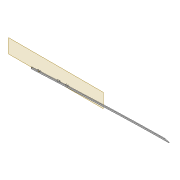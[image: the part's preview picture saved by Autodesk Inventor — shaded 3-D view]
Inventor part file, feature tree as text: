
AUTODESK INVENTOR PART (.ipt)
format: ipt  version: 2022 (Build 260153000, 153)  size: 629,760 bytes
history: native  units: mm
features: projected_geometry x9, extrude x8, sketch x8, fillet x2, shell x1, plane x1, chamfer x1
ambient origin geometry x8: Origin, YZ Plane, XZ Plane, XY Plane, X Axis, Y Axis, Z Axis, Center Point
bodies: Solid1 (feature_tree)
feature tree (30):
  extrude  "Extrusion1"  Depth=4.0mm
  shell  "Shell1"  Thickness=2.4mm
  extrude  "Extrusion8"  Depth=5.9mm
  extrude  "Extrusion3"  Depth=10.0mm TaperAngle=0.0deg
  extrude  "Extrusion4"  Depth=5.0mm
  fillet  "Fillet1"  Radius=5.0mm
  sketch  "Sketch10"  dims[d22=2.0mm d23=0.0mm d31=2.0mm d32=5.0mm]
  extrude  "Extrusion5"  Depth=2.5mm
  plane  "Work Plane2"
  extrude  "Extrusion9"  Depth=5.0mm
  fillet  "Fillet2"  Radius=2.5mm
  extrude  "Extrusion10"  Depth=6.0mm
  chamfer  "Chamfer1"  Distance=2.0mm
  extrude  "Extrusion13"  Depth=5.0mm
  sketch  "Sketch31"  dims[d37=5.0mm d38=2.0mm d40=2.5mm]
  sketch  "Sketch35"  dims[d66=3.0mm d67=12.0mm d68=5.0mm d69=45.0mm d70=12.0mm d71=3.05mm d72=10.0mm d73=0.0mm d74=2.0mm d75=100.0mm d76=20.0mm d77=0.5mm d78=10.0mm d79=0.0mm d109=45.0deg d129=3.0mm d130=2.0mm d131=45.0deg d132=1.0mm d133=1.0mm d134=10.0mm d135=0.0mm d136=1.0mm d137=1.0mm d138=1.0mm d139=1.0mm d140=20.0mm]
  sketch  "Sketch3"  dims[d0=2.0mm d1=0.0mm d2=4.0mm d7=2.4mm]
  sketch  "Sketch8"  dims[d8=2.4mm d9=5.9mm]
  sketch  "Sketch9"  dims[d13=10.0mm d14=0.0mm d16=10.0mm d17=0.0mm]
  projected_geometry  "Projected Loop4"
  projected_geometry  "Projected Loop10"
  sketch  "Sketch24"  dims[d34=2.0mm d35=2.5mm]
  projected_geometry  "Projected Loop11"
  projected_geometry  "Projected Loop12"
  projected_geometry  "Projected Loop13"
  projected_geometry  "Projected Loop14"
  sketch  "Sketch32"  dims[d62=80.0mm d63=6.0mm d64=2.0mm d65=0.0mm]
  projected_geometry  "Project Cut Edges3"
  projected_geometry  "Project Cut Edges5"
  projected_geometry  "Project Cut Edges7"
